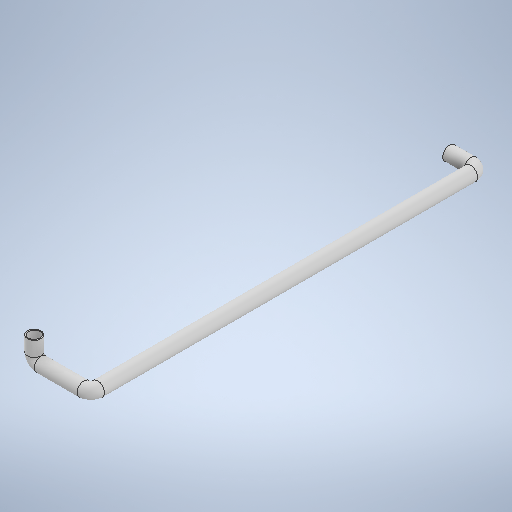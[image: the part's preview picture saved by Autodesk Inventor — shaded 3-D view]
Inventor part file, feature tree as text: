
AUTODESK INVENTOR PART (.ipt)
format: ipt  version: 2025.2 (Build 292293000, 293)  size: 279,040 bytes
history: native  units: mm
features: sketch x2, plane x1, sweep x1
ambient origin geometry x8: Origin, YZ Plane, XZ Plane, XY Plane, X Axis, Y Axis, Z Axis, Center Point
bodies: Solid1 (feature_tree)
feature tree (4):
  sketch  "3D Sketch1"
  plane  "Work Plane1"
  sweep  "Sweep1"
  sketch  "Sketch1"  dims[d0=6.497mm d1=3.0mm d2=90.0deg d3=18.5mm d4=90.0deg d5=161.75mm d6=90.0deg d7=9.25mm d8=6.0mm d9=5.0mm d10=0.0mm d11=0.0mm]
